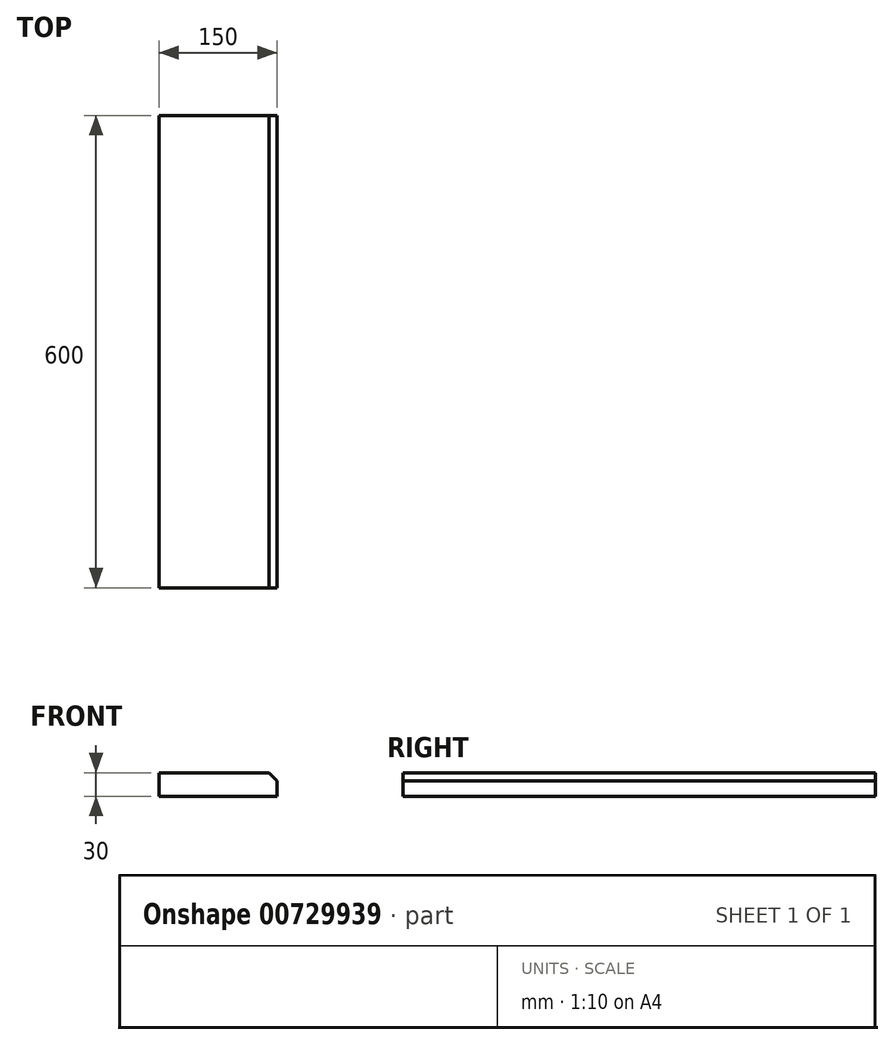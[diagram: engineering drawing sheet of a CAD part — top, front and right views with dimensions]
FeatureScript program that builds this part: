
annotation { "Feature Type Name" : "Feature", "Feature Type Description" : "" }
export const myFeature = defineFeature(function(context is Context, id is Id, definition is map)
    precondition{}
    {
        {
            var Q0;
            Q0=qCreatedBy(makeId("Front.planeOp"),FACE);
            var sketch = newSketch(context, id + "F0", { "sketchPlane" : qUnion([Q0])});
            skLineSegment(sketch, "E0", {"start": v(0, 0) * mm, "end": v(-150, 0) * mm});
            skLineSegment(sketch, "E1", {"start": v(-150, 0) * mm, "end": v(-150, 30) * mm});
            skLineSegment(sketch, "E2", {"start": v(-150, 30) * mm, "end": v(-10, 30) * mm});
            skLineSegment(sketch, "E3", {"start": v(-10, 30) * mm, "end": v(0, 20) * mm});
            skLineSegment(sketch, "E4", {"start": v(0, 20) * mm, "end": v(0, 0) * mm});
            skSolve(sketch);
        }
        {
            var Q0;
            Q0 = qSketchRegion(id + "F0", true);
            extrude(context, id + "F1", {"entities" : qUnion([Q0]), "depth" : 600 * mm, "offsetDistance" : 25 * mm, "symmetric" : true});
        }
    });
